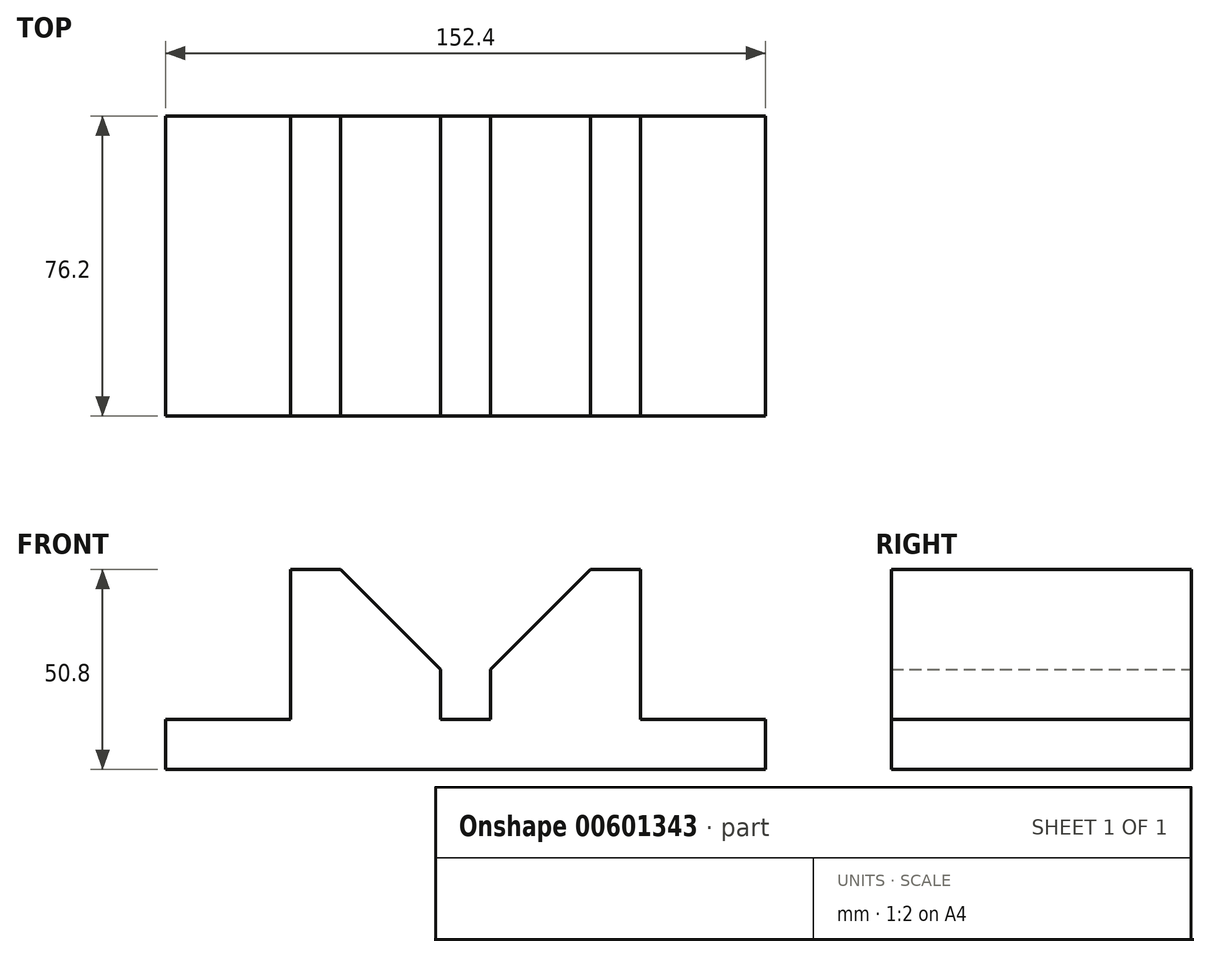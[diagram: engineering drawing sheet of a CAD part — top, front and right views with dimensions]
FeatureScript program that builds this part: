
annotation { "Feature Type Name" : "Feature", "Feature Type Description" : "" }
export const myFeature = defineFeature(function(context is Context, id is Id, definition is map)
    precondition{}
    {
        {
            var Q0;
            Q0=qCreatedBy(makeId("Front.planeOp"),FACE);
            var sketch = newSketch(context, id + "F0", { "sketchPlane" : qUnion([Q0])});
            skLineSegment(sketch, "E0", {"start": v(-75.97, 20.4) * mm, "end": v(76.43, 20.4) * mm});
            skLineSegment(sketch, "E1", {"start": v(76.43, 20.4) * mm, "end": v(76.43, 33.1) * mm});
            skLineSegment(sketch, "E2", {"start": v(76.43, 33.1) * mm, "end": v(44.68, 33.1) * mm});
            skLineSegment(sketch, "E3", {"start": v(44.68, 33.1) * mm, "end": v(44.68, 71.2) * mm});
            skLineSegment(sketch, "E4.MirrorCS", {"start": v(-44.22, 33.1) * mm, "end": v(-44.22, 71.2) * mm});
            skLineSegment(sketch, "E5.MirrorCS", {"start": v(-75.97, 33.1) * mm, "end": v(-44.22, 33.1) * mm});
            skLineSegment(sketch, "E6.MirrorCS", {"start": v(-75.97, 20.4) * mm, "end": v(-75.97, 33.1) * mm});
            skLineSegment(sketch, "E7", {"start": v(-44.22, 71.2) * mm, "end": v(-31.52, 71.2) * mm});
            skLineSegment(sketch, "E8", {"start": v(-6.12, 33.1) * mm, "end": v(-6.12, 45.8) * mm});
            skLineSegment(sketch, "E9", {"start": v(-6.12, 45.8) * mm, "end": v(-31.52, 71.2) * mm});
            skLineSegment(sketch, "E10", {"start": v(-6.12, 33.1) * mm, "end": v(6.58, 33.1) * mm});
            skLineSegment(sketch, "E11", {"start": v(6.58, 33.1) * mm, "end": v(6.58, 45.8) * mm});
            skLineSegment(sketch, "E12", {"start": v(44.68, 71.2) * mm, "end": v(31.98, 71.2) * mm});
            skLineSegment(sketch, "E13", {"start": v(31.98, 71.2) * mm, "end": v(6.58, 45.8) * mm});
            skSolve(sketch);
        }
        {
            var Q0;
            Q0=makeQuery(id+"F0.imprint","IMPRINT",FACE,{"disambiguationData":[TD([[makeQuery(id+"F0.imprint","IMPRINT",EDGE,{"derivedFrom":sQuery(id+"F0.wireOp",EDGE,"E0")}),1.0]])]});
            extrude(context, id + "F1", {"entities" : qUnion([Q0]), "depth" : 76.2 * mm, "offsetDistance" : 25.4 * mm});
        }
    });
